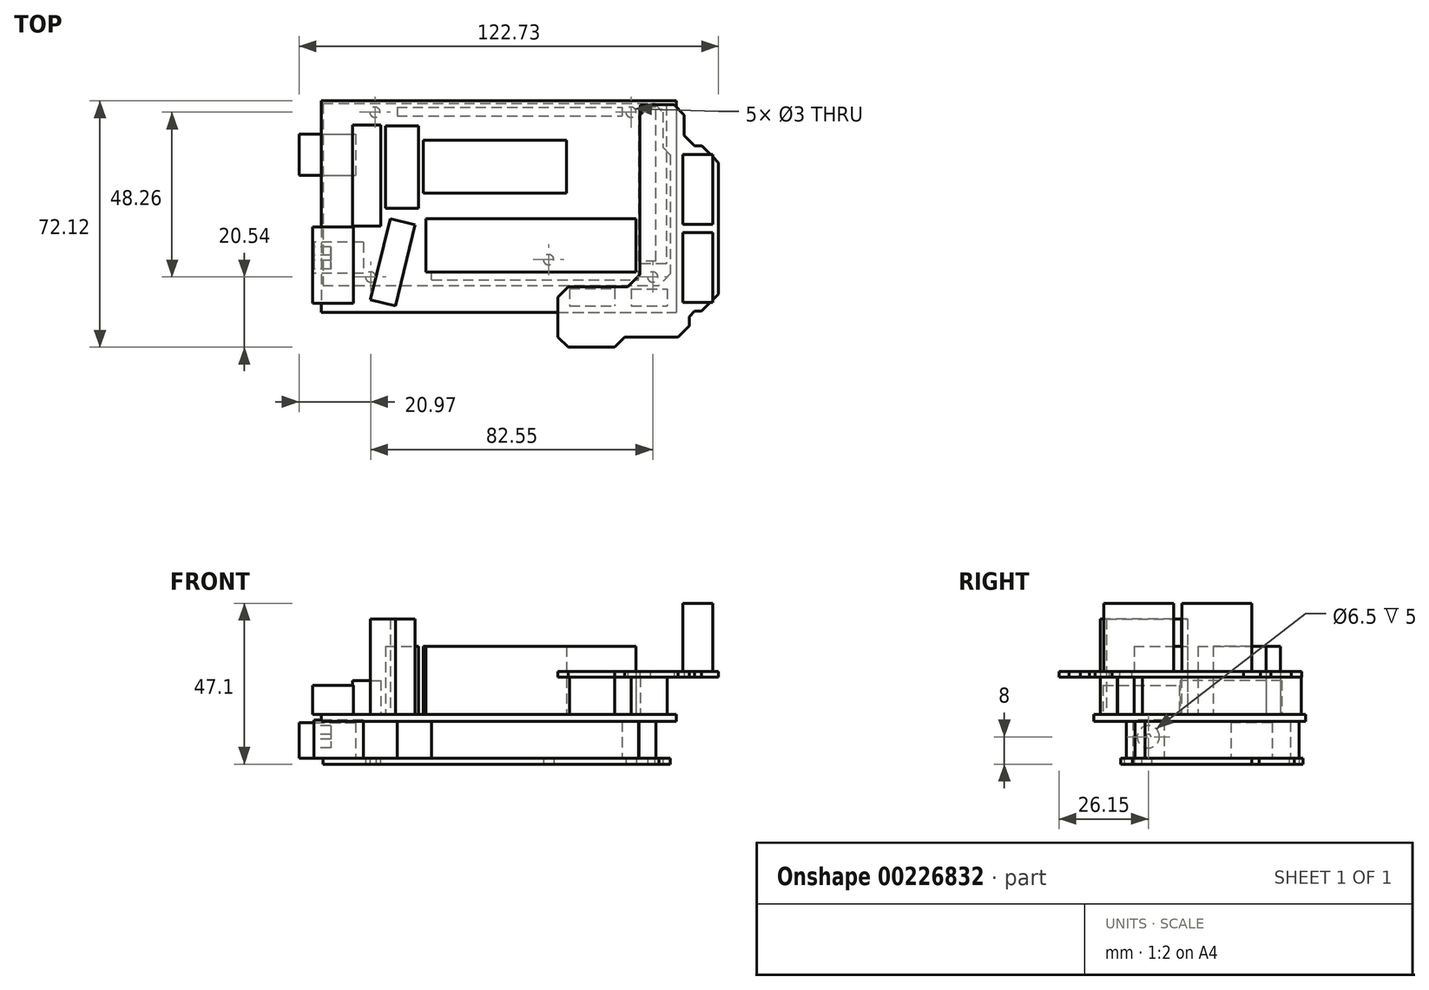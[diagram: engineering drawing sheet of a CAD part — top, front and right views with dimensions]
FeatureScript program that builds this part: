
annotation { "Feature Type Name" : "Feature", "Feature Type Description" : "" }
export const myFeature = defineFeature(function(context is Context, id is Id, definition is map)
    precondition{}
    {
        {
            var Q0;
            Q0=qCreatedBy(makeId("Top.planeOp"),FACE);
            var sketch = newSketch(context, id + "F0", { "sketchPlane" : qUnion([Q0])});
            skLineSegment(sketch, "E0.bottom", {"start": v(0, 0) * mm, "end": v(101.6, 0) * mm});
            skLineSegment(sketch, "E0.top", {"start": v(0, -53.34) * mm, "end": v(101.6, -53.34) * mm});
            skLineSegment(sketch, "E0.left", {"start": v(0, 0) * mm, "end": v(0, -53.34) * mm});
            skLineSegment(sketch, "E0.right", {"start": v(101.6, 0) * mm, "end": v(101.6, -53.34) * mm});
            skCircle(sketch, "E1", {"center": v(13.97, -50.8) * mm, "radius": 1.5 * mm});
            skCircle(sketch, "E2", {"center": v(96.52, -50.8) * mm, "radius": 1.5 * mm});
            skCircle(sketch, "E3", {"center": v(90.17, -2.54) * mm, "radius": 1.5 * mm});
            skCircle(sketch, "E4", {"center": v(15.24, -2.54) * mm, "radius": 1.5 * mm});
            skCircle(sketch, "E5", {"center": v(66.04, -45.72) * mm, "radius": 1.5 * mm});
            skLineSegment(sketch, "E6", {"start": v(0, -2.54) * mm, "end": v(101.6, -2.54) * mm, "construction": true});
            skLineSegment(sketch, "E7", {"start": v(0, -50.8) * mm, "end": v(101.6, -50.8) * mm, "construction": true});
            skLineSegment(sketch, "E8", {"start": v(101.6, -49.88) * mm, "end": v(98.34, -53.34) * mm});
            skLineSegment(sketch, "E9", {"start": v(97.1, 0) * mm, "end": v(99.41, -2.54) * mm});
            skLineSegment(sketch, "E10", {"start": v(99.41, -2.54) * mm, "end": v(99.41, -12.76) * mm});
            skLineSegment(sketch, "E11", {"start": v(99.41, -12.76) * mm, "end": v(101.6, -14.98) * mm});
            skSolve(sketch);
        }
        {
            var Q0;
            {var subQ3=sQuery(id+"F0.wireOp",EDGE,"E0.left");Q0=makeQuery(id+"F0.imprint","IMPRINT",FACE,{"disambiguationData":[TD([[makeQuery(id+"F0.imprint","IMPRINT",EDGE,{"derivedFrom":subQ3}),1.0]])]});}
            extrude(context, id + "F1", {"entities" : qUnion([Q0]), "depth" : 1.7 * mm});
        }
        {
            var Q0;
            Q0=makeQuery(id+"F1.opExtrude","CAP_FACE",FACE,{"disambiguationData":[OSD([sQuery(id+"F0.wireOp",EDGE,"E0.bottom"),sQuery(id+"F0.wireOp",EDGE,"E0.top"),sQuery(id+"F0.wireOp",EDGE,"E0.left"),sQuery(id+"F0.wireOp",EDGE,"E0.right"),sQuery(id+"F0.wireOp",EDGE,"E1"),sQuery(id+"F0.wireOp",EDGE,"E2"),sQuery(id+"F0.wireOp",EDGE,"E3"),sQuery(id+"F0.wireOp",EDGE,"E4"),sQuery(id+"F0.wireOp",EDGE,"E5"),sQuery(id+"F0.wireOp",EDGE,"E8"),sQuery(id+"F0.wireOp",EDGE,"E9"),sQuery(id+"F0.wireOp",EDGE,"E10"),sQuery(id+"F0.wireOp",EDGE,"E11")])],"isStart":false});
            var sketch = newSketch(context, id + "F2", { "sketchPlane" : qUnion([Q0])});
            skLineSegment(sketch, "E12.bottom", {"start": v(-7, -9) * mm, "end": v(9.5, -9) * mm});
            skLineSegment(sketch, "E12.top", {"start": v(-7, -21) * mm, "end": v(9.5, -21) * mm});
            skLineSegment(sketch, "E12.left", {"start": v(-7, -9) * mm, "end": v(-7, -21) * mm});
            skLineSegment(sketch, "E12.right", {"start": v(9.5, -9) * mm, "end": v(9.5, -21) * mm});
            skLineSegment(sketch, "E13.0", {"start": v(0, 0) * mm, "end": v(0, -53.34) * mm, "construction": true});
            skLineSegment(sketch, "E14.0", {"start": v(0, -53.34) * mm, "end": v(98.34, -53.34) * mm, "construction": true});
            skLineSegment(sketch, "E15.0", {"start": v(101.6, -14.98) * mm, "end": v(101.6, -49.88) * mm, "construction": true});
            skLineSegment(sketch, "E16.bottom", {"start": v(11.8, -40.64) * mm, "end": v(-2.7, -40.64) * mm});
            skLineSegment(sketch, "E16.top", {"start": v(11.8, -49.74) * mm, "end": v(-2.7, -49.74) * mm});
            skLineSegment(sketch, "E16.left", {"start": v(11.8, -40.64) * mm, "end": v(11.8, -49.74) * mm});
            skLineSegment(sketch, "E16.right", {"start": v(-2.7, -40.64) * mm, "end": v(-2.7, -49.74) * mm});
            skLineSegment(sketch, "E17.bottom", {"start": v(21.7, -1.1) * mm, "end": v(87.55, -1.1) * mm});
            skLineSegment(sketch, "E17.top", {"start": v(21.7, -3.64) * mm, "end": v(87.55, -3.64) * mm});
            skLineSegment(sketch, "E17.left", {"start": v(21.7, -1.1) * mm, "end": v(21.7, -3.64) * mm});
            skLineSegment(sketch, "E17.right", {"start": v(87.55, -1.1) * mm, "end": v(87.55, -3.64) * mm});
            skLineSegment(sketch, "E18.bottom", {"start": v(31.8, -51.64) * mm, "end": v(92.3, -51.64) * mm});
            skLineSegment(sketch, "E18.top", {"start": v(31.8, -49.1) * mm, "end": v(92.3, -49.1) * mm});
            skLineSegment(sketch, "E18.left", {"start": v(31.8, -51.64) * mm, "end": v(31.8, -49.1) * mm});
            skLineSegment(sketch, "E18.right", {"start": v(92.3, -51.64) * mm, "end": v(92.3, -49.1) * mm});
            skLineSegment(sketch, "E19.bottom", {"start": v(97.5, -46.14) * mm, "end": v(92.5, -46.14) * mm});
            skLineSegment(sketch, "E19.top", {"start": v(97.5, -1.14) * mm, "end": v(92.5, -1.14) * mm});
            skLineSegment(sketch, "E19.left", {"start": v(97.5, -46.14) * mm, "end": v(97.5, -1.14) * mm});
            skLineSegment(sketch, "E19.right", {"start": v(92.5, -46.14) * mm, "end": v(92.5, -1.14) * mm});
            skSolve(sketch);
        }
        {
            var Q0;
            {var subQ0=sQuery(id+"F2.wireOp",EDGE,"E16.left");Q0=makeQuery(id+"F2.imprint","IMPRINT",FACE,{"disambiguationData":[TD([[makeQuery(id+"F2.imprint","IMPRINT",EDGE,{"derivedFrom":subQ0}),-1.0]])]});}
            var Q1;
            {var subQ0=sQuery(id+"F2.wireOp",EDGE,"E16.right");Q1=makeQuery(id+"F2.imprint","IMPRINT",FACE,{"disambiguationData":[TD([[makeQuery(id+"F2.imprint","IMPRINT",EDGE,{"derivedFrom":subQ0}),1.0]])]});}
            extrude(context, id + "F3", {"entities" : qUnion([Q0, Q1]), "depth" : 11.2 * mm});
        }
        {
            var Q0;
            Q0=makeQuery(id+"F3.opExtrude","SWEPT_FACE",FACE,{"disambiguationData":[OSD([sQuery(id+"F2.wireOp",EDGE,"E16.right")])]});
            var sketch = newSketch(context, id + "F4", { "sketchPlane" : qUnion([Q0])});
            skCircle(sketch, "E20", {"center": v(45.2, 8) * mm, "radius": 3.25 * mm});
            skCircle(sketch, "E21", {"center": v(45.2, 8) * mm, "radius": 0.75 * mm});
            skSolve(sketch);
        }
        {
            var Q0;
            Q0=makeQuery(id+"F4.imprint","IMPRINT",FACE,{"disambiguationData":[TD([[makeQuery(id+"F4.imprint","IMPRINT",EDGE,{"derivedFrom":sQuery(id+"F4.wireOp",EDGE,"E20")}),1.0]])]});
            extrude(context, id + "F5", {"entities" : qUnion([Q0]), "operationType" : NewBodyOperationType.REMOVE, "oppositeDirection" : true, "depth" : 5 * mm});
        }
        {
            var Q0;
            {var subQ0=sQuery(id+"F2.wireOp",EDGE,"E12.right");Q0=makeQuery(id+"F2.imprint","IMPRINT",FACE,{"disambiguationData":[TD([[makeQuery(id+"F2.imprint","IMPRINT",EDGE,{"derivedFrom":subQ0}),-1.0]])]});}
            var Q1;
            {var subQ0=sQuery(id+"F2.wireOp",EDGE,"E12.left");Q1=makeQuery(id+"F2.imprint","IMPRINT",FACE,{"disambiguationData":[TD([[makeQuery(id+"F2.imprint","IMPRINT",EDGE,{"derivedFrom":subQ0}),1.0]])]});}
            extrude(context, id + "F6", {"entities" : qUnion([Q0, Q1]), "depth" : 10.5 * mm});
        }
        {
            var Q0;
            Q0=makeQuery(id+"F2.imprint","IMPRINT",FACE,{"disambiguationData":[TD([[makeQuery(id+"F2.imprint","IMPRINT",EDGE,{"derivedFrom":sQuery(id+"F2.wireOp",EDGE,"E17.bottom")}),-1.0]])]});
            var Q1;
            Q1=makeQuery(id+"F2.imprint","IMPRINT",FACE,{"disambiguationData":[TD([[makeQuery(id+"F2.imprint","IMPRINT",EDGE,{"derivedFrom":sQuery(id+"F2.wireOp",EDGE,"E19.bottom")}),-1.0]])]});
            var Q2;
            Q2=makeQuery(id+"F2.imprint","IMPRINT",FACE,{"disambiguationData":[TD([[makeQuery(id+"F2.imprint","IMPRINT",EDGE,{"derivedFrom":sQuery(id+"F2.wireOp",EDGE,"E18.bottom")}),1.0]])]});
            extrude(context, id + "F7", {"entities" : qUnion([Q0, Q1, Q2]), "depth" : 10.8 * mm});
        }
        {
            var Q0;
            Q0=makeQuery(id+"F7.opExtrude","CAP_FACE",FACE,{"disambiguationData":[OSD([sQuery(id+"F2.wireOp",EDGE,"E19.bottom"),sQuery(id+"F2.wireOp",EDGE,"E19.top"),sQuery(id+"F2.wireOp",EDGE,"E19.left"),sQuery(id+"F2.wireOp",EDGE,"E19.right")])],"isStart":false});
            cPlane(context, id + "F8", {"entities" : qUnion([Q0]), "cplaneType" : CPlaneType.OFFSET, "offset" : 0 * mm, "width" : 150 * mm, "height" : 150 * mm});
        }
        {
            var Q0;
            Q0=qCreatedBy(id+"F8.planeOp",FACE);
            var sketch = newSketch(context, id + "F9", { "sketchPlane" : qUnion([Q0])});
            skLineSegment(sketch, "E22.bottom", {"start": v(-0.53, 0.78) * mm, "end": v(103.37, 0.78) * mm});
            skLineSegment(sketch, "E22.top", {"start": v(-0.53, -61.12) * mm, "end": v(103.37, -61.12) * mm});
            skLineSegment(sketch, "E22.left", {"start": v(-0.53, 0.78) * mm, "end": v(-0.53, -61.12) * mm});
            skLineSegment(sketch, "E22.right", {"start": v(103.37, 0.78) * mm, "end": v(103.37, -61.12) * mm});
            skLineSegment(sketch, "E23.0", {"start": v(0, 0) * mm, "end": v(97.1, 0) * mm, "construction": true});
            skLineSegment(sketch, "E24.0", {"start": v(0, 0) * mm, "end": v(0, -53.34) * mm, "construction": true});
            skLineSegment(sketch, "E25.0", {"start": v(97.1, 0) * mm, "end": v(99.41, -2.54) * mm, "construction": true});
            skLineSegment(sketch, "E26.0", {"start": v(99.41, -2.54) * mm, "end": v(99.41, -12.76) * mm, "construction": true});
            skLineSegment(sketch, "E27.0", {"start": v(99.41, -12.76) * mm, "end": v(101.6, -14.98) * mm, "construction": true});
            skLineSegment(sketch, "E28.0", {"start": v(101.6, -14.98) * mm, "end": v(101.6, -49.88) * mm, "construction": true});
            skLineSegment(sketch, "E29.0", {"start": v(101.6, -49.88) * mm, "end": v(98.34, -53.34) * mm, "construction": true});
            skLineSegment(sketch, "E30.0", {"start": v(0, -53.34) * mm, "end": v(98.34, -53.34) * mm, "construction": true});
            skSolve(sketch);
        }
        {
            var Q0;
            Q0=qSketchRegion(id+"F9",true);
            extrude(context, id + "F10", {"entities" : qUnion([Q0]), "depth" : 2 * mm});
        }
        {
            var Q0;
            Q0=makeQuery(id+"F10.opExtrude","CAP_FACE",FACE,{"disambiguationData":[OSD([sQuery(id+"F9.wireOp",EDGE,"E22.bottom"),sQuery(id+"F9.wireOp",EDGE,"E22.top"),sQuery(id+"F9.wireOp",EDGE,"E22.left"),sQuery(id+"F9.wireOp",EDGE,"E22.right")])],"isStart":false});
            var sketch = newSketch(context, id + "F11", { "sketchPlane" : qUnion([Q0])});
            skLineSegment(sketch, "E31.bottom", {"start": v(8.98, -58.47) * mm, "end": v(-3.01, -58.47) * mm});
            skLineSegment(sketch, "E31.top", {"start": v(8.98, -36.15) * mm, "end": v(-3.01, -36.15) * mm});
            skLineSegment(sketch, "E31.left", {"start": v(8.98, -58.47) * mm, "end": v(8.98, -36.15) * mm});
            skLineSegment(sketch, "E31.right", {"start": v(-3.01, -58.47) * mm, "end": v(-3.01, -36.15) * mm});
            skLineSegment(sketch, "E32.bottom", {"start": v(8.65, -6.23) * mm, "end": v(16.94, -6.23) * mm});
            skLineSegment(sketch, "E32.top", {"start": v(8.65, -35.93) * mm, "end": v(16.94, -35.93) * mm});
            skLineSegment(sketch, "E32.left", {"start": v(8.65, -6.23) * mm, "end": v(8.65, -35.93) * mm});
            skLineSegment(sketch, "E32.right", {"start": v(16.94, -6.23) * mm, "end": v(16.94, -35.93) * mm});
            skLineSegment(sketch, "E33.bottom", {"start": v(18.29, -30.7) * mm, "end": v(27.95, -30.7) * mm});
            skLineSegment(sketch, "E33.top", {"start": v(18.29, -6.5) * mm, "end": v(27.95, -6.5) * mm});
            skLineSegment(sketch, "E33.left", {"start": v(18.29, -30.7) * mm, "end": v(18.29, -6.5) * mm});
            skLineSegment(sketch, "E33.right", {"start": v(27.95, -30.7) * mm, "end": v(27.95, -6.5) * mm});
            skLineSegment(sketch, "E34.bottom", {"start": v(29.4, -10.76) * mm, "end": v(71.33, -10.76) * mm});
            skLineSegment(sketch, "E34.top", {"start": v(29.4, -26.26) * mm, "end": v(71.33, -26.26) * mm});
            skLineSegment(sketch, "E34.left", {"start": v(29.4, -10.76) * mm, "end": v(29.4, -26.26) * mm});
            skLineSegment(sketch, "E34.right", {"start": v(71.33, -10.76) * mm, "end": v(71.33, -26.26) * mm});
            skLineSegment(sketch, "E35.bottom", {"start": v(30.11, -49.37) * mm, "end": v(91.54, -49.37) * mm});
            skLineSegment(sketch, "E35.top", {"start": v(30.11, -33.68) * mm, "end": v(91.54, -33.68) * mm});
            skLineSegment(sketch, "E35.left", {"start": v(30.11, -49.37) * mm, "end": v(30.11, -33.68) * mm});
            skLineSegment(sketch, "E35.right", {"start": v(91.54, -49.37) * mm, "end": v(91.54, -33.68) * mm});
            skLineSegment(sketch, "E36.bottom", {"start": v(41.17, -52.49) * mm, "end": v(51.14, -52.49) * mm});
            skLineSegment(sketch, "E36.top", {"start": v(41.17, -60.1) * mm, "end": v(51.14, -60.1) * mm});
            skLineSegment(sketch, "E36.left", {"start": v(41.17, -52.49) * mm, "end": v(41.17, -60.1) * mm});
            skLineSegment(sketch, "E36.right", {"start": v(51.14, -52.49) * mm, "end": v(51.14, -60.1) * mm});
            skLineSegment(sketch, "E37.bottom", {"start": v(56.46, -54.2) * mm, "end": v(66.6, -54.2) * mm});
            skLineSegment(sketch, "E37.top", {"start": v(56.46, -59.28) * mm, "end": v(66.6, -59.28) * mm});
            skLineSegment(sketch, "E37.left", {"start": v(56.46, -54.2) * mm, "end": v(56.46, -59.28) * mm});
            skLineSegment(sketch, "E37.right", {"start": v(66.6, -54.2) * mm, "end": v(66.6, -59.28) * mm});
            skLineSegment(sketch, "E38.bottom", {"start": v(72.17, -54.24) * mm, "end": v(85.35, -54.24) * mm});
            skLineSegment(sketch, "E38.top", {"start": v(72.17, -59.28) * mm, "end": v(85.35, -59.28) * mm});
            skLineSegment(sketch, "E38.left", {"start": v(72.17, -54.24) * mm, "end": v(72.17, -59.28) * mm});
            skLineSegment(sketch, "E38.right", {"start": v(85.35, -54.24) * mm, "end": v(85.35, -59.28) * mm});
            skLineSegment(sketch, "E39.bottom", {"start": v(90.2, -54.29) * mm, "end": v(100.77, -54.29) * mm});
            skLineSegment(sketch, "E39.top", {"start": v(90.2, -59.28) * mm, "end": v(100.77, -59.28) * mm});
            skLineSegment(sketch, "E39.left", {"start": v(90.2, -54.29) * mm, "end": v(90.2, -59.28) * mm});
            skLineSegment(sketch, "E39.right", {"start": v(100.77, -54.29) * mm, "end": v(100.77, -59.28) * mm});
            skLineSegment(sketch, "E40.bottom", {"start": v(76.22, -28.9) * mm, "end": v(86.41, -28.9) * mm});
            skLineSegment(sketch, "E40.top", {"start": v(76.22, -33.68) * mm, "end": v(86.41, -33.68) * mm});
            skLineSegment(sketch, "E40.left", {"start": v(76.22, -28.9) * mm, "end": v(76.22, -33.68) * mm});
            skLineSegment(sketch, "E40.right", {"start": v(86.41, -28.9) * mm, "end": v(86.41, -33.68) * mm});
            skLineSegment(sketch, "E41.bottom", {"start": v(90.8, -2.97) * mm, "end": v(73.24, -2.97) * mm});
            skLineSegment(sketch, "E41.top", {"start": v(90.8, -12.92) * mm, "end": v(73.24, -12.92) * mm});
            skLineSegment(sketch, "E41.left", {"start": v(90.8, -2.97) * mm, "end": v(90.8, -12.92) * mm});
            skLineSegment(sketch, "E41.right", {"start": v(73.24, -2.97) * mm, "end": v(73.24, -12.92) * mm});
            skLineSegment(sketch, "E42", {"start": v(19.71, -33.73) * mm, "end": v(26.99, -35.5) * mm});
            skLineSegment(sketch, "E43", {"start": v(26.99, -35.5) * mm, "end": v(21.18, -59.26) * mm});
            skLineSegment(sketch, "E44", {"start": v(21.18, -59.26) * mm, "end": v(13.87, -57.47) * mm});
            skLineSegment(sketch, "E45", {"start": v(13.87, -57.47) * mm, "end": v(19.71, -33.73) * mm});
            skLineSegment(sketch, "E46.bottom", {"start": v(100.47, -0.46) * mm, "end": v(92.9, -0.46) * mm});
            skLineSegment(sketch, "E46.top", {"start": v(100.47, -46.9) * mm, "end": v(92.9, -46.9) * mm});
            skLineSegment(sketch, "E46.left", {"start": v(100.47, -0.46) * mm, "end": v(100.47, -46.9) * mm});
            skLineSegment(sketch, "E46.right", {"start": v(92.9, -0.46) * mm, "end": v(92.9, -46.9) * mm});
            skSolve(sketch);
        }
        {
            var Q0;
            {var subQ0=sQuery(id+"F11.wireOp",EDGE,"E31.right");Q0=makeQuery(id+"F11.imprint","IMPRINT",FACE,{"disambiguationData":[TD([[makeQuery(id+"F11.imprint","IMPRINT",EDGE,{"derivedFrom":subQ0}),-1.0]])]});}
            var Q1;
            {var subQ0=sQuery(id+"F11.wireOp",EDGE,"E31.left");var subQ1=sQuery(id+"F11.wireOp",EDGE,"E31.bottom");var subQ2=makeQuery(id+"F11.imprint","INTERSECT",VERTEX,{"derivedFrom":[subQ1,subQ0]});Q1=makeQuery(id+"F11.imprint","IMPRINT",FACE,{"disambiguationData":[TD([[makeQuery(id+"F11.imprint","IMPRINT",EDGE,{"disambiguationData":[TD([[subQ2,-1.0]])],"derivedFrom":subQ1}),-1.0]])]});}
            extrude(context, id + "F12", {"entities" : qUnion([Q0, Q1]), "depth" : 8.5 * mm});
        }
        {
            var Q0;
            {var subQ6=sQuery(id+"F11.wireOp",EDGE,"E32.bottom");Q0=makeQuery(id+"F11.imprint","IMPRINT",FACE,{"disambiguationData":[TD([[makeQuery(id+"F11.imprint","IMPRINT",EDGE,{"derivedFrom":subQ6}),-1.0]])]});}
            extrude(context, id + "F13", {"entities" : qUnion([Q0]), "depth" : 10 * mm});
        }
        {
            var Q0;
            Q0=makeQuery(id+"F11.imprint","IMPRINT",FACE,{"disambiguationData":[TD([[makeQuery(id+"F11.imprint","IMPRINT",EDGE,{"derivedFrom":sQuery(id+"F11.wireOp",EDGE,"E33.bottom")}),1.0]])]});
            extrude(context, id + "F14", {"entities" : qUnion([Q0]), "depth" : 20 * mm});
        }
        {
            var Q0;
            Q0=makeQuery(id+"F11.imprint","IMPRINT",FACE,{"disambiguationData":[TD([[makeQuery(id+"F11.imprint","IMPRINT",EDGE,{"derivedFrom":sQuery(id+"F11.wireOp",EDGE,"E42")}),-1.0]])]});
            extrude(context, id + "F15", {"entities" : qUnion([Q0]), "depth" : 28 * mm});
        }
        {
            var Q0;
            Q0=makeQuery(id+"F11.imprint","IMPRINT",FACE,{"disambiguationData":[TD([[makeQuery(id+"F11.imprint","IMPRINT",EDGE,{"derivedFrom":sQuery(id+"F11.wireOp",EDGE,"E35.bottom")}),1.0]])]});
            var Q1;
            Q1=makeQuery(id+"F11.imprint","IMPRINT",FACE,{"disambiguationData":[TD([[makeQuery(id+"F11.imprint","IMPRINT",EDGE,{"derivedFrom":sQuery(id+"F11.wireOp",EDGE,"E34.bottom")}),-1.0]])]});
            extrude(context, id + "F16", {"entities" : qUnion([Q0, Q1]), "depth" : 20 * mm});
        }
        {
            var Q0;
            Q0=makeQuery(id+"F11.imprint","IMPRINT",FACE,{"disambiguationData":[TD([[makeQuery(id+"F11.imprint","IMPRINT",EDGE,{"derivedFrom":sQuery(id+"F11.wireOp",EDGE,"E38.bottom")}),-1.0]])]});
            var Q1;
            Q1=makeQuery(id+"F11.imprint","IMPRINT",FACE,{"disambiguationData":[TD([[makeQuery(id+"F11.imprint","IMPRINT",EDGE,{"derivedFrom":sQuery(id+"F11.wireOp",EDGE,"E39.bottom")}),-1.0]])]});
            var Q2;
            Q2=makeQuery(id+"F11.imprint","IMPRINT",FACE,{"disambiguationData":[TD([[makeQuery(id+"F11.imprint","IMPRINT",EDGE,{"derivedFrom":sQuery(id+"F11.wireOp",EDGE,"E46.bottom")}),1.0]])]});
            extrude(context, id + "F17", {"entities" : qUnion([Q0, Q1, Q2]), "depth" : 11 * mm});
        }
        {
            var Q0;
            Q0=makeQuery(id+"F17.opExtrude","CAP_FACE",FACE,{"disambiguationData":[OSD([sQuery(id+"F11.wireOp",EDGE,"E46.bottom"),sQuery(id+"F11.wireOp",EDGE,"E46.top"),sQuery(id+"F11.wireOp",EDGE,"E46.left"),sQuery(id+"F11.wireOp",EDGE,"E46.right")])],"isStart":false});
            cPlane(context, id + "F18", {"entities" : qUnion([Q0]), "cplaneType" : CPlaneType.OFFSET, "offset" : 0 * mm, "width" : 150 * mm, "height" : 150 * mm});
        }
        {
            var Q0;
            Q0=qCreatedBy(id+"F18.planeOp",FACE);
            var sketch = newSketch(context, id + "F19", { "sketchPlane" : qUnion([Q0])});
            skLineSegment(sketch, "E47", {"start": v(89.2, -53.7) * mm, "end": v(92.73, -50.15) * mm});
            skLineSegment(sketch, "E48", {"start": v(92.73, -50.15) * mm, "end": v(92.73, -3.36) * mm});
            skLineSegment(sketch, "E49", {"start": v(92.73, -3.36) * mm, "end": v(95.73, -0.35) * mm});
            skLineSegment(sketch, "E50", {"start": v(95.73, -0.35) * mm, "end": v(102.74, -0.35) * mm});
            skLineSegment(sketch, "E51", {"start": v(102.74, -0.35) * mm, "end": v(105.73, -3.35) * mm});
            skLineSegment(sketch, "E52", {"start": v(105.73, -3.35) * mm, "end": v(105.73, -9.35) * mm});
            skLineSegment(sketch, "E53", {"start": v(105.73, -9.35) * mm, "end": v(108.73, -12.35) * mm});
            skLineSegment(sketch, "E54", {"start": v(108.73, -12.35) * mm, "end": v(110.93, -12.35) * mm});
            skLineSegment(sketch, "E55", {"start": v(110.93, -12.35) * mm, "end": v(115.73, -17.35) * mm});
            skLineSegment(sketch, "E56", {"start": v(115.73, -17.35) * mm, "end": v(115.73, -55.8) * mm});
            skLineSegment(sketch, "E57", {"start": v(115.73, -55.8) * mm, "end": v(110.73, -60.8) * mm});
            skLineSegment(sketch, "E58", {"start": v(110.73, -60.8) * mm, "end": v(108.8, -60.8) * mm});
            skLineSegment(sketch, "E59", {"start": v(108.8, -60.8) * mm, "end": v(107.18, -62.42) * mm});
            skLineSegment(sketch, "E60", {"start": v(107.18, -62.42) * mm, "end": v(107.18, -65.1) * mm});
            skLineSegment(sketch, "E61", {"start": v(107.18, -65.1) * mm, "end": v(103.93, -68.35) * mm});
            skLineSegment(sketch, "E62", {"start": v(103.93, -68.35) * mm, "end": v(88.35, -68.35) * mm});
            skLineSegment(sketch, "E63", {"start": v(88.35, -68.35) * mm, "end": v(85.36, -71.34) * mm});
            skLineSegment(sketch, "E64", {"start": v(85.36, -71.34) * mm, "end": v(71.77, -71.34) * mm});
            skLineSegment(sketch, "E65", {"start": v(71.77, -71.34) * mm, "end": v(68.78, -68.35) * mm});
            skLineSegment(sketch, "E66", {"start": v(68.78, -68.35) * mm, "end": v(68.78, -56.72) * mm});
            skLineSegment(sketch, "E67", {"start": v(68.78, -56.72) * mm, "end": v(71.75, -53.7) * mm});
            skLineSegment(sketch, "E68", {"start": v(71.75, -53.7) * mm, "end": v(89.2, -53.7) * mm});
            skSolve(sketch);
        }
        {
            var Q0;
            Q0=qSketchRegion(id+"F19",true);
            extrude(context, id + "F20", {"entities" : qUnion([Q0]), "depth" : 1.6 * mm});
        }
        {
            var Q0;
            Q0=makeQuery(id+"F20.opExtrude","CAP_FACE",FACE,{"disambiguationData":[OSD([sQuery(id+"F19.wireOp",EDGE,"E47"),sQuery(id+"F19.wireOp",EDGE,"E48"),sQuery(id+"F19.wireOp",EDGE,"E49"),sQuery(id+"F19.wireOp",EDGE,"E50"),sQuery(id+"F19.wireOp",EDGE,"E51"),sQuery(id+"F19.wireOp",EDGE,"E52"),sQuery(id+"F19.wireOp",EDGE,"E53"),sQuery(id+"F19.wireOp",EDGE,"E54"),sQuery(id+"F19.wireOp",EDGE,"E55"),sQuery(id+"F19.wireOp",EDGE,"E56"),sQuery(id+"F19.wireOp",EDGE,"E57"),sQuery(id+"F19.wireOp",EDGE,"E58"),sQuery(id+"F19.wireOp",EDGE,"E59"),sQuery(id+"F19.wireOp",EDGE,"E60"),sQuery(id+"F19.wireOp",EDGE,"E61"),sQuery(id+"F19.wireOp",EDGE,"E62"),sQuery(id+"F19.wireOp",EDGE,"E63"),sQuery(id+"F19.wireOp",EDGE,"E64"),sQuery(id+"F19.wireOp",EDGE,"E65"),sQuery(id+"F19.wireOp",EDGE,"E66"),sQuery(id+"F19.wireOp",EDGE,"E67"),sQuery(id+"F19.wireOp",EDGE,"E68")])],"isStart":false});
            var sketch = newSketch(context, id + "F21", { "sketchPlane" : qUnion([Q0])});
            skLineSegment(sketch, "E69.bottom", {"start": v(105.27, -35.35) * mm, "end": v(114.08, -35.35) * mm});
            skLineSegment(sketch, "E69.top", {"start": v(105.27, -14.95) * mm, "end": v(114.08, -14.95) * mm});
            skLineSegment(sketch, "E69.left", {"start": v(105.27, -35.35) * mm, "end": v(105.27, -14.95) * mm});
            skLineSegment(sketch, "E69.right", {"start": v(114.08, -35.35) * mm, "end": v(114.08, -14.95) * mm});
            skLineSegment(sketch, "E70.bottom", {"start": v(105.27, -37.8) * mm, "end": v(114.08, -37.8) * mm});
            skLineSegment(sketch, "E70.top", {"start": v(105.27, -58.2) * mm, "end": v(114.08, -58.2) * mm});
            skLineSegment(sketch, "E70.left", {"start": v(105.27, -37.8) * mm, "end": v(105.27, -58.2) * mm});
            skLineSegment(sketch, "E70.right", {"start": v(114.08, -37.8) * mm, "end": v(114.08, -58.2) * mm});
            skSolve(sketch);
        }
        {
            var Q0;
            {var subQ0=sQuery(id+"F21.wireOp",EDGE,"E69.right");var subQ1=sQuery(id+"F21.wireOp",EDGE,"E69.top");var subQ2=makeQuery(id+"F21.imprint","INTERSECT",VERTEX,{"derivedFrom":[subQ1,subQ0]});Q0=makeQuery(id+"F21.imprint","IMPRINT",FACE,{"disambiguationData":[TD([[makeQuery(id+"F21.imprint","IMPRINT",EDGE,{"disambiguationData":[TD([[subQ2,1.0]])],"derivedFrom":subQ1}),-1.0]])]});}
            var Q1;
            {var subQ1=sQuery(id+"F21.wireOp",EDGE,"E69.bottom");Q1=makeQuery(id+"F21.imprint","IMPRINT",FACE,{"disambiguationData":[TD([[makeQuery(id+"F21.imprint","IMPRINT",EDGE,{"derivedFrom":subQ1}),1.0]])]});}
            var Q2;
            {var subQ0=sQuery(id+"F21.wireOp",EDGE,"E70.right");var subQ1=sQuery(id+"F21.wireOp",EDGE,"E70.top");var subQ2=makeQuery(id+"F21.imprint","INTERSECT",VERTEX,{"derivedFrom":[subQ1,subQ0]});Q2=makeQuery(id+"F21.imprint","IMPRINT",FACE,{"disambiguationData":[TD([[makeQuery(id+"F21.imprint","IMPRINT",EDGE,{"disambiguationData":[TD([[subQ2,1.0]])],"derivedFrom":subQ1}),1.0]])]});}
            var Q3;
            {var subQ1=sQuery(id+"F21.wireOp",EDGE,"E70.bottom");Q3=makeQuery(id+"F21.imprint","IMPRINT",FACE,{"disambiguationData":[TD([[makeQuery(id+"F21.imprint","IMPRINT",EDGE,{"derivedFrom":subQ1}),-1.0]])]});}
            extrude(context, id + "F22", {"entities" : qUnion([Q0, Q1, Q2, Q3]), "operationType" : NewBodyOperationType.ADD, "depth" : 20 * mm});
        }
    });
